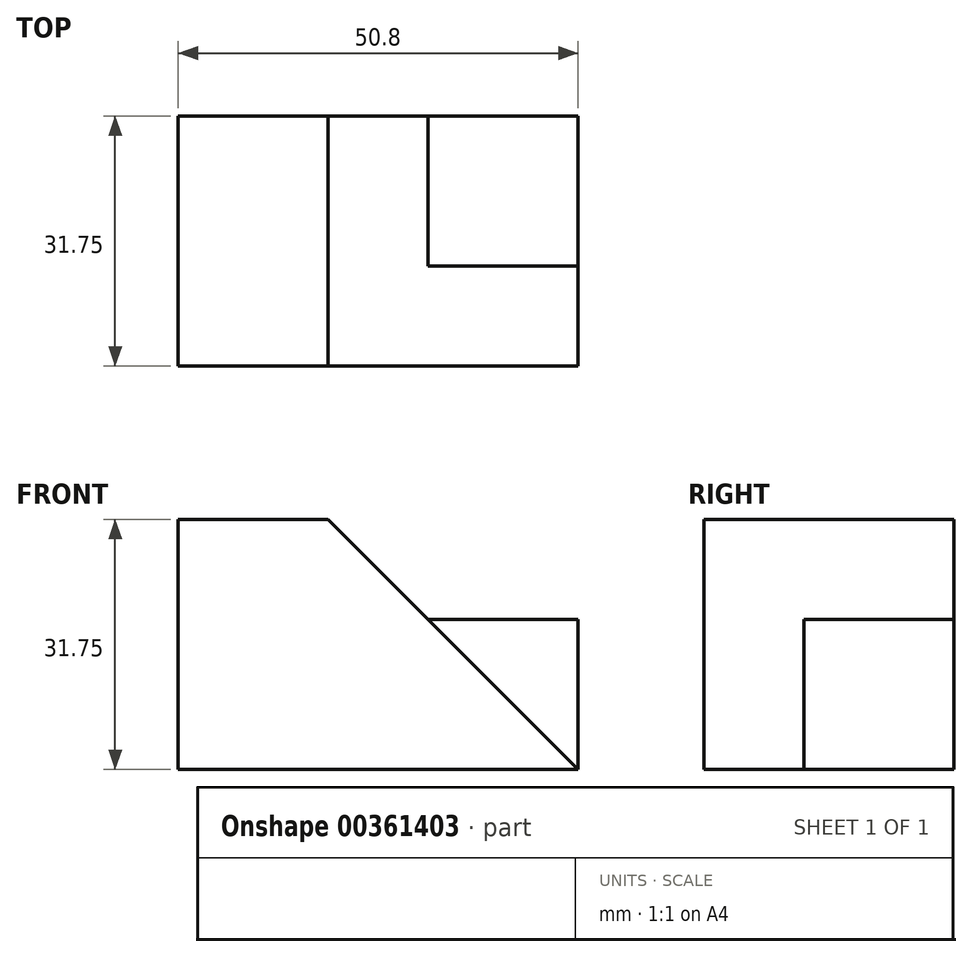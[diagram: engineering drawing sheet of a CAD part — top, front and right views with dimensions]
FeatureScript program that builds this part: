
annotation { "Feature Type Name" : "Feature", "Feature Type Description" : "" }
export const myFeature = defineFeature(function(context is Context, id is Id, definition is map)
    precondition{}
    {
        {
            var Q0;
            Q0=qCreatedBy(makeId("Front.planeOp"),FACE);
            var sketch = newSketch(context, id + "F0", { "sketchPlane" : qUnion([Q0])});
            skLineSegment(sketch, "E0", {"start": v(0, 0) * mm, "end": v(0, 31.75) * mm});
            skLineSegment(sketch, "E1", {"start": v(0, 31.75) * mm, "end": v(19.05, 31.75) * mm});
            skLineSegment(sketch, "E2", {"start": v(0, 0) * mm, "end": v(50.8, 0) * mm});
            skLineSegment(sketch, "E3", {"start": v(50.8, 0) * mm, "end": v(19.05, 31.75) * mm});
            skSolve(sketch);
        }
        {
            var Q0;
            Q0 = qSketchRegion(id + "F0", true);
            extrude(context, id + "F1", {"entities" : qUnion([Q0]), "depth" : 31.75 * mm});
        }
        {
            var Q0;
            Q0=makeQuery(id+"F1.opExtrude","CAP_FACE",FACE,{"disambiguationData":[OSD([sQuery(id+"F0.wireOp",EDGE,"E0"),sQuery(id+"F0.wireOp",EDGE,"E1"),sQuery(id+"F0.wireOp",EDGE,"E2"),sQuery(id+"F0.wireOp",EDGE,"E3")])],"isStart":true});
            var sketch = newSketch(context, id + "F2", { "sketchPlane" : qUnion([Q0])});
            skLineSegment(sketch, "E4.bottom", {"start": v(-50.8, 0) * mm, "end": v(-50.8, 0) * mm});
            skLineSegment(sketch, "E4.top", {"start": v(-50.8, 19.05) * mm, "end": v(-50.8, 19.05) * mm});
            skLineSegment(sketch, "E4.left", {"start": v(-50.8, 0) * mm, "end": v(-50.8, 19.05) * mm});
            skLineSegment(sketch, "E4.right", {"start": v(-50.8, 0) * mm, "end": v(-50.8, 19.05) * mm});
            skLineSegment(sketch, "E5.bottom", {"start": v(-50.8, 19.05) * mm, "end": v(-31.75, 19.05) * mm});
            skLineSegment(sketch, "E5.top", {"start": v(-50.8, 19.05) * mm, "end": v(-31.75, 19.05) * mm});
            skLineSegment(sketch, "E5.right", {"start": v(-31.75, 19.05) * mm, "end": v(-31.75, 19.05) * mm});
            skLineSegment(sketch, "E6.bottom", {"start": v(-31.75, 0) * mm, "end": v(-50.8, 0) * mm});
            skLineSegment(sketch, "E6.top", {"start": v(-31.75, 0) * mm, "end": v(-50.8, 0) * mm});
            skLineSegment(sketch, "E6.left", {"start": v(-31.75, 0) * mm, "end": v(-31.75, 0) * mm});
            skLineSegment(sketch, "E7", {"start": v(-31.75, 19.05) * mm, "end": v(-31.75, 0) * mm});
            skSolve(sketch);
        }
        {
            var Q0;
            Q0 = qSketchRegion(id + "F2", true);
            extrude(context, id + "F3", {"entities" : qUnion([Q0]), "operationType" : NewBodyOperationType.ADD, "oppositeDirection" : true, "depth" : 19.05 * mm});
        }
    });
